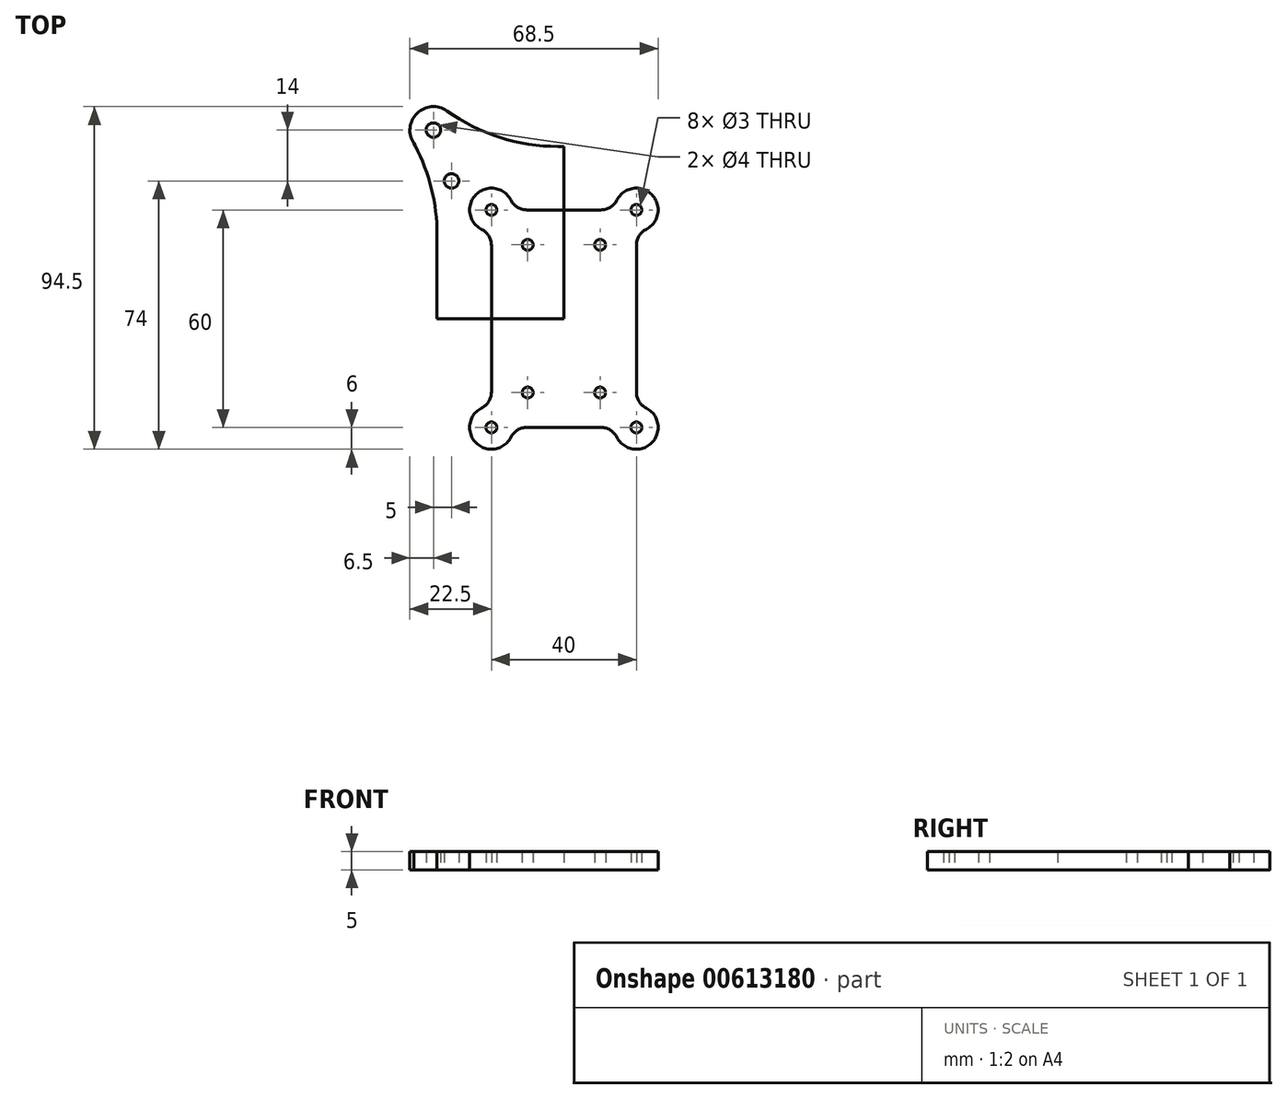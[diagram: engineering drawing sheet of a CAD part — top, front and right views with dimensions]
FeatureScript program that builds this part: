
annotation { "Feature Type Name" : "Feature", "Feature Type Description" : "" }
export const myFeature = defineFeature(function(context is Context, id is Id, definition is map)
    precondition{}
    {
        {
            var Q0;
            Q0=qCreatedBy(makeId("Top.planeOp"),FACE);
            var sketch = newSketch(context, id + "F0", { "sketchPlane" : qUnion([Q0])});
            skLineSegment(sketch, "E0.top", {"start": v(0, 30) * mm, "end": v(-10.2, 30) * mm});
            skLineSegment(sketch, "E0.left", {"start": v(0, 0) * mm, "end": v(0, 30) * mm});
            skLineSegment(sketch, "E0.right", {"start": v(-20, 0) * mm, "end": v(-20, 20.2) * mm});
            skArc(sketch, "E1", {"start": v(-14.66, 32.73) * mm, "mid": v(-24.24, 34.24) * mm, "end": v(-22.73, 24.66) * mm});
            skCircle(sketch, "E2", {"center": v(-20, 30) * mm, "radius": 1.5 * mm});
            skCircle(sketch, "E3", {"center": v(-10, 20.37) * mm, "radius": 1.5 * mm});
            skLineSegment(sketch, "E4.MirrorCS", {"start": v(0, 30) * mm, "end": v(10.2, 30) * mm});
            skCircle(sketch, "E5.MirrorC", {"center": v(20, 30) * mm, "radius": 1.5 * mm});
            skArc(sketch, "E6.MirrorCS", {"start": v(14.66, 32.73) * mm, "mid": v(24.24, 34.24) * mm, "end": v(22.73, 24.66) * mm});
            skLineSegment(sketch, "E7.MirrorCS", {"start": v(20, 0) * mm, "end": v(20, 20.2) * mm});
            skCircle(sketch, "E8.MirrorC", {"center": v(10, 20.37) * mm, "radius": 1.5 * mm});
            skArc(sketch, "E9.MirrorCS", {"start": v(-14.66, -32.73) * mm, "mid": v(-24.24, -34.24) * mm, "end": v(-22.73, -24.66) * mm});
            skLineSegment(sketch, "E10.MirrorCS", {"start": v(0, -30) * mm, "end": v(-10.2, -30) * mm});
            skCircle(sketch, "E11.MirrorC", {"center": v(-20, -30) * mm, "radius": 1.5 * mm});
            skCircle(sketch, "E12.MirrorC", {"center": v(-10, -20.37) * mm, "radius": 1.5 * mm});
            skCircle(sketch, "E13.MirrorC", {"center": v(20, -30) * mm, "radius": 1.5 * mm});
            skArc(sketch, "E14.MirrorCS", {"start": v(14.66, -32.73) * mm, "mid": v(24.24, -34.24) * mm, "end": v(22.73, -24.66) * mm});
            skLineSegment(sketch, "E15.MirrorCS", {"start": v(0, -30) * mm, "end": v(10.2, -30) * mm});
            skCircle(sketch, "E16.MirrorC", {"center": v(10, -20.37) * mm, "radius": 1.5 * mm});
            skLineSegment(sketch, "E17.MirrorCS", {"start": v(-20, 0) * mm, "end": v(-20, -20.2) * mm});
            skLineSegment(sketch, "E18.MirrorCS", {"start": v(20, 0) * mm, "end": v(20, -20.2) * mm});
            skPoint(sketch, "E19.visualSharp", {"position": v(-20, 24) * mm});
            skArc(sketch, "E19.filletArc", {"start": v(-20, 20.2) * mm, "mid": v(-20.74, 22.81) * mm, "end": v(-22.73, 24.66) * mm});
            skPoint(sketch, "E20.visualSharp", {"position": v(-14, 30) * mm});
            skArc(sketch, "E20.filletArc", {"start": v(-14.66, 32.73) * mm, "mid": v(-12.81, 30.74) * mm, "end": v(-10.2, 30) * mm});
            skPoint(sketch, "E21.visualSharp", {"position": v(14, 30) * mm});
            skArc(sketch, "E21.filletArc", {"start": v(10.2, 30) * mm, "mid": v(12.81, 30.74) * mm, "end": v(14.66, 32.73) * mm});
            skPoint(sketch, "E22.visualSharp", {"position": v(20, 24) * mm});
            skArc(sketch, "E22.filletArc", {"start": v(22.73, 24.66) * mm, "mid": v(20.74, 22.81) * mm, "end": v(20, 20.2) * mm});
            skPoint(sketch, "E23.visualSharp", {"position": v(20, -24) * mm});
            skArc(sketch, "E23.filletArc", {"start": v(20, -20.2) * mm, "mid": v(20.74, -22.81) * mm, "end": v(22.73, -24.66) * mm});
            skPoint(sketch, "E24.visualSharp", {"position": v(14, -30) * mm});
            skArc(sketch, "E24.filletArc", {"start": v(14.66, -32.73) * mm, "mid": v(12.81, -30.74) * mm, "end": v(10.2, -30) * mm});
            skPoint(sketch, "E25.visualSharp", {"position": v(-14, -30) * mm});
            skArc(sketch, "E25.filletArc", {"start": v(-10.2, -30) * mm, "mid": v(-12.81, -30.74) * mm, "end": v(-14.66, -32.73) * mm});
            skPoint(sketch, "E26.visualSharp", {"position": v(-20, -24) * mm});
            skArc(sketch, "E26.filletArc", {"start": v(-22.73, -24.66) * mm, "mid": v(-20.74, -22.81) * mm, "end": v(-20, -20.2) * mm});
            skSolve(sketch);
        }
        {
            var Q0;
            Q0=makeQuery(id+"F0.imprint","IMPRINT",FACE,{"disambiguationData":[TD([[makeQuery(id+"F0.imprint","IMPRINT",EDGE,{"derivedFrom":sQuery(id+"F0.wireOp",EDGE,"E0.top")}),1.0]])]});
            extrude(context, id + "F1", {"entities" : qUnion([Q0]), "depth" : 5 * mm, "offsetDistance" : 25 * mm});
        }
        {
            var Q0;
            Q0=qCreatedBy(makeId("Top.planeOp"),FACE);
            var sketch = newSketch(context, id + "F2", { "sketchPlane" : qUnion([Q0])});
            skLineSegment(sketch, "E27.bottom", {"start": v(-19.9, 47.5) * mm, "end": v(0, 47.5) * mm});
            skLineSegment(sketch, "E27.left", {"start": v(-35, 36.2) * mm, "end": v(-35, 0) * mm});
            skCircle(sketch, "E28", {"center": v(-36, 52) * mm, "radius": 2 * mm});
            skLineSegment(sketch, "E29", {"start": v(0, 47.5) * mm, "end": v(0, 0) * mm});
            skLineSegment(sketch, "E30", {"start": v(0, 0) * mm, "end": v(-35, 0) * mm});
            skCircle(sketch, "E31", {"center": v(-31, 38) * mm, "radius": 2 * mm});
            skArc(sketch, "E32", {"start": v(-41.36, 48.32) * mm, "mid": v(-40.24, 56.93) * mm, "end": v(-31.56, 56.75) * mm});
            skLineSegment(sketch, "E33", {"start": v(-41.36, 48.32) * mm, "end": v(-35, 36.2) * mm});
            skLineSegment(sketch, "E34", {"start": v(-19.9, 47.5) * mm, "end": v(-31.56, 56.75) * mm});
            skSolve(sketch);
        }
        {
            var Q0;
            Q0=makeQuery(id+"F2.imprint","IMPRINT",FACE,{"disambiguationData":[TD([[makeQuery(id+"F2.imprint","IMPRINT",EDGE,{"derivedFrom":sQuery(id+"F2.wireOp",EDGE,"E27.bottom")}),-1.0]])]});
            var Q1;
            Q1=makeQuery(id+"FbhvTWJwiDD6F1E_1.1.F2.imprint","IMPRINT",FACE,{"disambiguationData":[TD([[makeQuery(id+"FbhvTWJwiDD6F1E_1.1.F2.imprint","IMPRINT",EDGE,{"derivedFrom":sQuery(id+"FbhvTWJwiDD6F1E_1.1.F2.wireOp",EDGE,"E27.bottom")}),-1.0]])]});
            var Q2;
            Q2=makeQuery(id+"Fr46HOGC9WjdyHn_1.1.FbhvTWJwiDD6F1E_1.1.F2.imprint","IMPRINT",FACE,{"disambiguationData":[TD([[makeQuery(id+"Fr46HOGC9WjdyHn_1.1.FbhvTWJwiDD6F1E_1.1.F2.imprint","IMPRINT",EDGE,{"derivedFrom":sQuery(id+"Fr46HOGC9WjdyHn_1.1.FbhvTWJwiDD6F1E_1.1.F2.wireOp",EDGE,"E27.bottom")}),-1.0]])]});
            var Q3;
            Q3=makeQuery(id+"Fr46HOGC9WjdyHn_1.1.F2.imprint","IMPRINT",FACE,{"disambiguationData":[TD([[makeQuery(id+"Fr46HOGC9WjdyHn_1.1.F2.imprint","IMPRINT",EDGE,{"derivedFrom":sQuery(id+"Fr46HOGC9WjdyHn_1.1.F2.wireOp",EDGE,"E27.bottom")}),-1.0]])]});
            extrude(context, id + "F3", {"entities" : qUnion([Q0, Q1, Q2, Q3]), "depth" : 5 * mm, "offsetDistance" : 25 * mm});
        }
        {
            var Q0;
            Q0=makeQuery(id+"F3.opExtrude","SWEPT_EDGE",EDGE,{"disambiguationData":[OSD([sQuery(id+"F2.wireOp",EDGE,"E27.bottom"),sQuery(id+"F2.wireOp",EDGE,"E34")])]});
            var Q1;
            Q1=makeQuery(id+"F3.opExtrude","SWEPT_EDGE",EDGE,{"disambiguationData":[OSD([sQuery(id+"F2.wireOp",EDGE,"E27.left"),sQuery(id+"F2.wireOp",EDGE,"E33")])]});
            var Q2;
            Q2=makeQuery(id+"F3.opExtrude","SWEPT_EDGE",EDGE,{"disambiguationData":[OSD([sQuery(id+"FbhvTWJwiDD6F1E_1.1.F2.wireOp",EDGE,"E27.left"),sQuery(id+"FbhvTWJwiDD6F1E_1.1.F2.wireOp",EDGE,"E33")])]});
            var Q3;
            Q3=makeQuery(id+"F3.opExtrude","SWEPT_EDGE",EDGE,{"disambiguationData":[OSD([sQuery(id+"FbhvTWJwiDD6F1E_1.1.F2.wireOp",EDGE,"E27.bottom"),sQuery(id+"FbhvTWJwiDD6F1E_1.1.F2.wireOp",EDGE,"E34")])]});
            var Q4;
            Q4=makeQuery(id+"F3.opExtrude","SWEPT_EDGE",EDGE,{"disambiguationData":[OSD([sQuery(id+"Fr46HOGC9WjdyHn_1.1.FbhvTWJwiDD6F1E_1.1.F2.wireOp",EDGE,"E27.left"),sQuery(id+"Fr46HOGC9WjdyHn_1.1.FbhvTWJwiDD6F1E_1.1.F2.wireOp",EDGE,"E33")])]});
            var Q5;
            Q5=makeQuery(id+"F3.opExtrude","SWEPT_EDGE",EDGE,{"disambiguationData":[OSD([sQuery(id+"Fr46HOGC9WjdyHn_1.1.FbhvTWJwiDD6F1E_1.1.F2.wireOp",EDGE,"E27.bottom"),sQuery(id+"Fr46HOGC9WjdyHn_1.1.FbhvTWJwiDD6F1E_1.1.F2.wireOp",EDGE,"E34")])]});
            var Q6;
            Q6=makeQuery(id+"F3.opExtrude","SWEPT_EDGE",EDGE,{"disambiguationData":[OSD([sQuery(id+"Fr46HOGC9WjdyHn_1.1.F2.wireOp",EDGE,"E27.bottom"),sQuery(id+"Fr46HOGC9WjdyHn_1.1.F2.wireOp",EDGE,"E34")])]});
            var Q7;
            Q7=makeQuery(id+"F3.opExtrude","SWEPT_EDGE",EDGE,{"disambiguationData":[OSD([sQuery(id+"Fr46HOGC9WjdyHn_1.1.F2.wireOp",EDGE,"E27.left"),sQuery(id+"Fr46HOGC9WjdyHn_1.1.F2.wireOp",EDGE,"E33")])]});
            fillet(context, id + "F4", {"entities" : qUnion([Q0, Q1, Q2, Q3, Q4, Q5, Q6, Q7]), "radius" : 52.8 * mm, "tangentPropagation" : true, "allowEdgeOverflow" : false});
        }
    });
